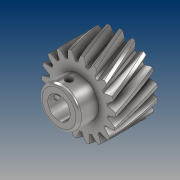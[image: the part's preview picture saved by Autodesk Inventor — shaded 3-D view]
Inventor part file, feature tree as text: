
AUTODESK INVENTOR PART (.ipt)
format: ipt  version: 2021 (Build 250183000, 183)  size: 557,056 bytes
history: native  units: mm (DEFAULTED — no unit token found)
features: extrude x4, sketch x4, plane x3, other x3, projected_geometry x2, pattern_circular x1, fillet x1
ambient origin geometry x8: Origin, YZ Plane, XZ Plane, XY Plane, X Axis, Y Axis, Z Axis, Center Point
bodies: Solid1 (feature_tree)
feature tree (18):
  extrude  "Extrusion1"  Depth=15.0mm TaperAngle=0.0deg
  plane  "Work Plane2"
  plane  "Work Plane8"
  plane  "Work Plane9"
  other  "Spur Gear"
  sketch  "Sketch3"  dims[d16=59.86mm d17=0.0mm d34=1.745329mm]
  extrude  "Extrusion2"  Depth=10.0mm TaperAngle=0.0deg
  extrude  "Extrusion3"  Depth=1.745329mm TaperAngle=0.0deg
  extrude  "Extrusion4"  TaperAngle=0.0deg  [1 undecoded]
  pattern_circular  "Circular Pattern1"  [2 undecoded]
  fillet  "Fillet1"  Radius=59.86mm
  sketch  "Sketch1"  dims[d0=26.444mm d1=15.0mm d2=0.0mm]
  sketch  "Sketch2"  dims[d3=23.944mm d4=10.0mm d5=0.0mm]
  other  "Srf1"
  projected_geometry  "Projected Loop1"
  sketch  "Sketch4"  dims[d39=0.0mm d41=0.0mm d43=59.86mm d46=59.86mm d47=0.0mm d48=0.0mm d49=8.0mm d50=3.0mm d51=15.75mm d52=0.0mm d53=7.0mm d54=0.0mm d55=2.5mm d56=7.0mm d57=0.0mm d58=20.0mm d59=90.0deg d61=1.0mm]
  projected_geometry  "Projected Loop2"
  other  "Pitch Diameter"
note: 3 required parameter values undecoded (feature->parameter linkage not recoverable at this tier; creation-order binding heuristic only, values carry confidence <= 0.55)
